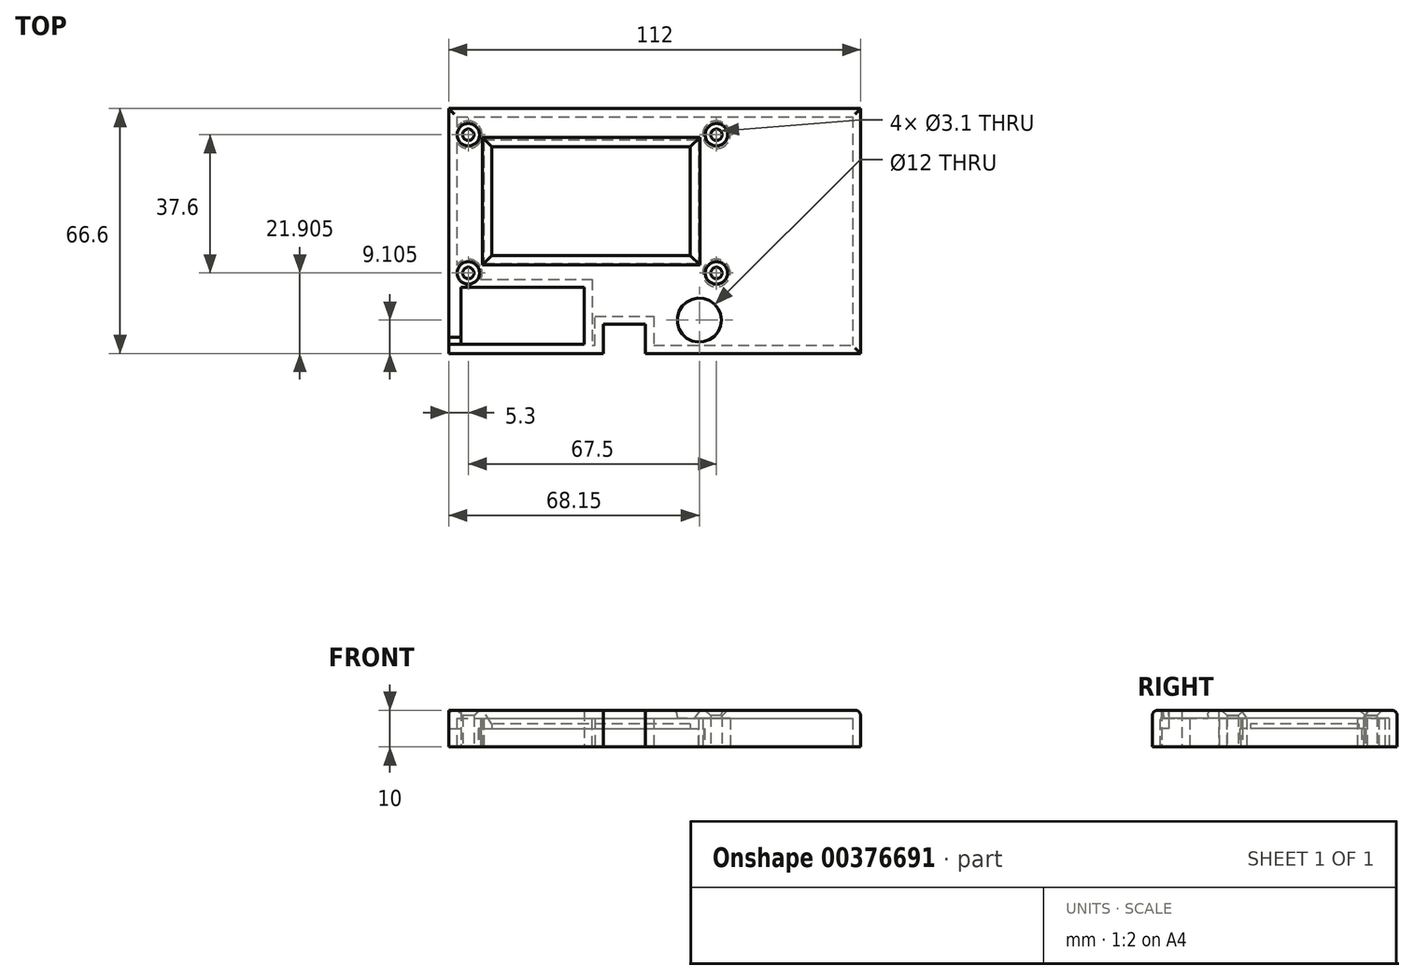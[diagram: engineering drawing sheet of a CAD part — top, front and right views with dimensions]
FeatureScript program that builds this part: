
annotation { "Feature Type Name" : "Feature", "Feature Type Description" : "" }
export const myFeature = defineFeature(function(context is Context, id is Id, definition is map)
    precondition{}
    {
        {
            var Q0;
            Q0=qCreatedBy(makeId("Top.planeOp"),FACE);
            var sketch = newSketch(context, id + "F0", { "sketchPlane" : qUnion([Q0])});
            skLineSegment(sketch, "E0.bottom", {"start": v(-50.5, 36.22) * mm, "end": v(61.5, 36.22) * mm});
            skLineSegment(sketch, "E0.top", {"start": v(-50.5, -30.38) * mm, "end": v(-8.5, -30.38) * mm});
            skLineSegment(sketch, "E0.left", {"start": v(-50.5, 36.22) * mm, "end": v(-50.5, -30.38) * mm});
            skLineSegment(sketch, "E0.right", {"start": v(61.5, 36.22) * mm, "end": v(61.5, -30.38) * mm});
            skLineSegment(sketch, "E1", {"start": v(-61.88, 29.12) * mm, "end": v(70.13, 29.12) * mm, "construction": true});
            skLineSegment(sketch, "E2", {"start": v(-64.5, -8.48) * mm, "end": v(70.13, -8.48) * mm, "construction": true});
            skLineSegment(sketch, "E3", {"start": v(-45.2, 39) * mm, "end": v(-45.2, -42.94) * mm, "construction": true});
            skLineSegment(sketch, "E4", {"start": v(22.3, 40.31) * mm, "end": v(22.3, -39.75) * mm, "construction": true});
            skLineSegment(sketch, "E5", {"start": v(17.65, -12.94) * mm, "end": v(17.65, -45.75) * mm, "construction": true});
            skLineSegment(sketch, "E6", {"start": v(-67.69, -21.28) * mm, "end": v(23.81, -21.28) * mm, "construction": true});
            skCircle(sketch, "E7", {"center": v(-45.2, 29.12) * mm, "radius": 1.55 * mm});
            skCircle(sketch, "E8", {"center": v(22.3, 29.12) * mm, "radius": 1.55 * mm});
            skCircle(sketch, "E9", {"center": v(-45.2, -8.48) * mm, "radius": 1.55 * mm});
            skCircle(sketch, "E10", {"center": v(22.3, -8.48) * mm, "radius": 1.55 * mm});
            skLineSegment(sketch, "E11.bottom", {"start": v(-38.8, 25.82) * mm, "end": v(15.2, 25.82) * mm});
            skLineSegment(sketch, "E11.top", {"start": v(-38.8, -3.68) * mm, "end": v(15.2, -3.68) * mm});
            skLineSegment(sketch, "E11.left", {"start": v(-38.8, 25.82) * mm, "end": v(-38.8, -3.68) * mm});
            skLineSegment(sketch, "E11.right", {"start": v(15.2, 25.82) * mm, "end": v(15.2, -3.68) * mm});
            skCircle(sketch, "E12", {"center": v(17.65, -21.28) * mm, "radius": 6 * mm});
            skLineSegment(sketch, "E13.bottom", {"start": v(-47.2, -12.38) * mm, "end": v(-13.7, -12.38) * mm});
            skLineSegment(sketch, "E13.top", {"start": v(-47.2, -27.88) * mm, "end": v(-13.7, -27.88) * mm});
            skLineSegment(sketch, "E13.left", {"start": v(-47.2, -12.38) * mm, "end": v(-47.2, -27.88) * mm});
            skLineSegment(sketch, "E13.right", {"start": v(-13.7, -12.38) * mm, "end": v(-13.7, -27.88) * mm});
            skLineSegment(sketch, "E14", {"start": v(-8.5, -30.38) * mm, "end": v(-8.5, -22.38) * mm});
            skLineSegment(sketch, "E15", {"start": v(3, -15.38) * mm, "end": v(3, -41.9) * mm, "construction": true});
            skLineSegment(sketch, "E16", {"start": v(-8.5, -22.38) * mm, "end": v(3, -22.38) * mm});
            skLineSegment(sketch, "E17", {"start": v(3, -22.38) * mm, "end": v(3, -30.38) * mm});
            skLineSegment(sketch, "E18.trimOffspring", {"start": v(3, -30.38) * mm, "end": v(61.5, -30.38) * mm});
            skLineSegment(sketch, "E19", {"start": v(-50.5, -27.89) * mm, "end": v(-47.2, -27.88) * mm});
            skLineSegment(sketch, "E20", {"start": v(-50.5, -25.89) * mm, "end": v(-47.2, -25.89) * mm});
            skSolve(sketch);
        }
        {
            var Q0;
            {var subQ7=sQuery(id+"F0.wireOp",EDGE,"E0.bottom");Q0=makeQuery(id+"F0.imprint","IMPRINT",FACE,{"disambiguationData":[TD([[makeQuery(id+"F0.imprint","IMPRINT",EDGE,{"derivedFrom":subQ7}),-1.0]])]});}
            var Q1;
            Q1=makeQuery(id+"F0.imprint","IMPRINT",FACE,{"disambiguationData":[TD([[makeQuery(id+"F0.imprint","IMPRINT",EDGE,{"derivedFrom":sQuery(id+"F0.wireOp",EDGE,"E12")}),1.0]])]});
            extrude(context, id + "F1", {"entities" : qUnion([Q0, Q1]), "depth" : 10 * mm});
        }
        {
            var Q0;
            {var subQ0=sQuery(id+"F0.wireOp",EDGE,"E19");Q0=makeQuery(id+"F0.imprint","IMPRINT",FACE,{"disambiguationData":[TD([[makeQuery(id+"F0.imprint","IMPRINT",EDGE,{"derivedFrom":subQ0}),1.0]])]});}
            extrude(context, id + "F2", {"entities" : qUnion([Q0]), "operationType" : NewBodyOperationType.ADD, "depth" : 5 * mm});
        }
        {
            var Q0;
            {var subQ0=sQuery(id+"F0.wireOp",EDGE,"E20");var subQ1=sQuery(id+"F0.wireOp",EDGE,"E19");var subQ2=sQuery(id+"F0.wireOp",EDGE,"E13.left");var subQ3=sQuery(id+"F0.wireOp",EDGE,"E0.left");Q0=makeQuery(id+"F2.boolean.opBoolean","MERGE",FACE,{"derivedFrom":[makeQuery(id+"F1.opExtrude","CAP_FACE",FACE,{"disambiguationData":[OSD([sQuery(id+"F0.wireOp",EDGE,"E0.bottom"),sQuery(id+"F0.wireOp",EDGE,"E0.top"),subQ3,sQuery(id+"F0.wireOp",EDGE,"E0.right"),sQuery(id+"F0.wireOp",EDGE,"E7"),sQuery(id+"F0.wireOp",EDGE,"E8"),sQuery(id+"F0.wireOp",EDGE,"E9"),sQuery(id+"F0.wireOp",EDGE,"E10"),sQuery(id+"F0.wireOp",EDGE,"E11.bottom"),sQuery(id+"F0.wireOp",EDGE,"E11.top"),sQuery(id+"F0.wireOp",EDGE,"E11.left"),sQuery(id+"F0.wireOp",EDGE,"E11.right"),sQuery(id+"F0.wireOp",EDGE,"E13.bottom"),sQuery(id+"F0.wireOp",EDGE,"E13.top"),subQ2,sQuery(id+"F0.wireOp",EDGE,"E13.right"),sQuery(id+"F0.wireOp",EDGE,"E14"),sQuery(id+"F0.wireOp",EDGE,"E16"),sQuery(id+"F0.wireOp",EDGE,"E17"),sQuery(id+"F0.wireOp",EDGE,"E18.trimOffspring"),subQ1,subQ0])],"isStart":true}),makeQuery(id+"F2.opExtrude","CAP_FACE",FACE,{"disambiguationData":[OSD([subQ3,subQ2,subQ1,subQ0])],"isStart":true})]});}
            shell(context, id + "F3", {"entities" : qUnion([Q0]), "thickness" : 2.2 * mm});
        }
        {
            var Q0;
            Q0=makeQuery(id+"F1.opExtrude","CAP_EDGE",EDGE,{"disambiguationData":[OSD([sQuery(id+"F0.wireOp",EDGE,"E11.right")])],"isStart":false});
            var Q1;
            Q1=makeQuery(id+"F1.opExtrude","CAP_EDGE",EDGE,{"disambiguationData":[OSD([sQuery(id+"F0.wireOp",EDGE,"E11.bottom")])],"isStart":false});
            var Q2;
            Q2=makeQuery(id+"F1.opExtrude","CAP_EDGE",EDGE,{"disambiguationData":[OSD([sQuery(id+"F0.wireOp",EDGE,"E11.top")])],"isStart":false});
            var Q3;
            Q3=makeQuery(id+"F1.opExtrude","CAP_EDGE",EDGE,{"disambiguationData":[OSD([sQuery(id+"F0.wireOp",EDGE,"E11.left")])],"isStart":false});
            chamfer(context, id + "F4", {"entities" : qUnion([Q0, Q1, Q2, Q3]), "chamferType" : ChamferType.OFFSET_ANGLE, "width" : 2.6 * mm, "oppositeDirection" : false, "angle" : 55 * degree, "tangentPropagation" : true});
        }
        {
            var Q0;
            {var subQ7=sQuery(id+"F0.wireOp",EDGE,"E0.bottom");Q0=makeQuery(id+"F0.imprint","IMPRINT",FACE,{"disambiguationData":[TD([[makeQuery(id+"F0.imprint","IMPRINT",EDGE,{"derivedFrom":subQ7}),-1.0]])]});}
            cPlane(context, id + "F5", {"entities" : qUnion([Q0]), "cplaneType" : CPlaneType.OFFSET, "offset" : 0 * mm, "width" : 150 * mm, "height" : 150 * mm});
        }
        {
            var Q0;
            Q0=qCreatedBy(id+"F5.planeOp",FACE);
            var sketch = newSketch(context, id + "F6", { "sketchPlane" : qUnion([Q0])});
            skLineSegment(sketch, "E21.bottom", {"start": v(-42.5, -6.57) * mm, "end": v(19.06, -6.57) * mm});
            skLineSegment(sketch, "E21.top", {"start": v(-42.5, 27.72) * mm, "end": v(19.06, 27.72) * mm});
            skLineSegment(sketch, "E21.left", {"start": v(-42.5, -6.57) * mm, "end": v(-42.5, 27.72) * mm});
            skLineSegment(sketch, "E21.right", {"start": v(19.06, -6.57) * mm, "end": v(19.06, 27.72) * mm});
            skSolve(sketch);
        }
        {
            var Q0;
            Q0=makeQuery(id+"F6.imprint","IMPRINT",FACE,{"disambiguationData":[TD([[makeQuery(id+"F6.imprint","IMPRINT",EDGE,{"derivedFrom":sQuery(id+"F6.wireOp",EDGE,"E21.bottom")}),1.0]])]});
            extrude(context, id + "F7", {"entities" : qUnion([Q0]), "operationType" : NewBodyOperationType.REMOVE, "depth" : 5 * mm});
        }
        {
            var Q0;
            Q0=makeQuery(id+"F0.imprint","IMPRINT",FACE,{"disambiguationData":[TD([[makeQuery(id+"F0.imprint","IMPRINT",EDGE,{"derivedFrom":sQuery(id+"F0.wireOp",EDGE,"E12")}),1.0]])]});
            extrude(context, id + "F8", {"entities" : qUnion([Q0]), "operationType" : NewBodyOperationType.REMOVE, "depth" : 25 * mm});
        }
        {
            var Q0;
            Q0=makeQuery(id+"F1.opExtrude","CAP_EDGE",EDGE,{"disambiguationData":[OSD([sQuery(id+"F0.wireOp",EDGE,"E0.bottom")])],"isStart":false});
            var Q1;
            {var subQ0=sQuery(id+"F0.wireOp",EDGE,"E0.left");Q1=makeQuery(id+"F1.opExtrude","CAP_EDGE",EDGE,{"disambiguationData":[OSD([subQ0]),TDD([makeQuery(id+"F0.imprint","IMPRINT",EDGE,{"disambiguationData":[TD([[makeQuery(id+"F0.imprint","INTERSECT",VERTEX,{"derivedFrom":[sQuery(id+"F0.wireOp",EDGE,"E0.bottom"),subQ0]}),-1.0]])],"derivedFrom":subQ0})])],"isStart":false});}
            var Q2;
            Q2=makeQuery(id+"F1.opExtrude","CAP_EDGE",EDGE,{"disambiguationData":[OSD([sQuery(id+"F0.wireOp",EDGE,"E0.top")])],"isStart":false});
            var Q3;
            Q3=makeQuery(id+"F1.opExtrude","CAP_EDGE",EDGE,{"disambiguationData":[OSD([sQuery(id+"F0.wireOp",EDGE,"E18.trimOffspring")])],"isStart":false});
            var Q4;
            Q4=makeQuery(id+"F1.opExtrude","CAP_EDGE",EDGE,{"disambiguationData":[OSD([sQuery(id+"F0.wireOp",EDGE,"E0.right")])],"isStart":false});
            fillet(context, id + "F9", {"entities" : qUnion([Q0, Q1, Q2, Q3, Q4]), "radius" : 1.5 * mm, "tangentPropagation" : true, "allowEdgeOverflow" : false});
        }
        {
            var Q0;
            Q0=makeQuery(id+"F8.boolean.opBoolean","INTERSECT",EDGE,{"derivedFrom":[makeQuery(id+"F1.opExtrude","CAP_FACE",FACE,{"disambiguationData":[OSD([sQuery(id+"F0.wireOp",EDGE,"E0.bottom"),sQuery(id+"F0.wireOp",EDGE,"E0.top"),sQuery(id+"F0.wireOp",EDGE,"E0.left"),sQuery(id+"F0.wireOp",EDGE,"E0.right"),sQuery(id+"F0.wireOp",EDGE,"E7"),sQuery(id+"F0.wireOp",EDGE,"E8"),sQuery(id+"F0.wireOp",EDGE,"E9"),sQuery(id+"F0.wireOp",EDGE,"E10"),sQuery(id+"F0.wireOp",EDGE,"E11.bottom"),sQuery(id+"F0.wireOp",EDGE,"E11.top"),sQuery(id+"F0.wireOp",EDGE,"E11.left"),sQuery(id+"F0.wireOp",EDGE,"E11.right"),sQuery(id+"F0.wireOp",EDGE,"E13.bottom"),sQuery(id+"F0.wireOp",EDGE,"E13.top"),sQuery(id+"F0.wireOp",EDGE,"E13.left"),sQuery(id+"F0.wireOp",EDGE,"E13.right"),sQuery(id+"F0.wireOp",EDGE,"E14"),sQuery(id+"F0.wireOp",EDGE,"E16"),sQuery(id+"F0.wireOp",EDGE,"E17"),sQuery(id+"F0.wireOp",EDGE,"E18.trimOffspring"),sQuery(id+"F0.wireOp",EDGE,"E19"),sQuery(id+"F0.wireOp",EDGE,"E20")])],"isStart":false}),makeQuery(id+"F8.opExtrude","SWEPT_FACE",FACE,{"disambiguationData":[OSD([sQuery(id+"F0.wireOp",EDGE,"E12")])]})]});
            fillet(context, id + "F10", {"entities" : qUnion([Q0]), "radius" : 1.5 * mm, "tangentPropagation" : true, "rho" : .5, "crossSection" : FilletCrossSection.CONIC, "allowEdgeOverflow" : false});
        }
        {
            var Q0;
            Q0=makeQuery(id+"F1.opExtrude","CAP_EDGE",EDGE,{"disambiguationData":[OSD([sQuery(id+"F0.wireOp",EDGE,"E9")])],"isStart":false});
            var Q1;
            Q1=makeQuery(id+"F1.opExtrude","CAP_EDGE",EDGE,{"disambiguationData":[OSD([sQuery(id+"F0.wireOp",EDGE,"E7")])],"isStart":false});
            var Q2;
            Q2=makeQuery(id+"F1.opExtrude","CAP_EDGE",EDGE,{"disambiguationData":[OSD([sQuery(id+"F0.wireOp",EDGE,"E8")])],"isStart":false});
            var Q3;
            Q3=makeQuery(id+"F1.opExtrude","CAP_EDGE",EDGE,{"disambiguationData":[OSD([sQuery(id+"F0.wireOp",EDGE,"E10")])],"isStart":false});
            chamfer(context, id + "F11", {"entities" : qUnion([Q0, Q1, Q2, Q3]), "width" : 1.5 * mm, "tangentPropagation" : true});
        }
    });
